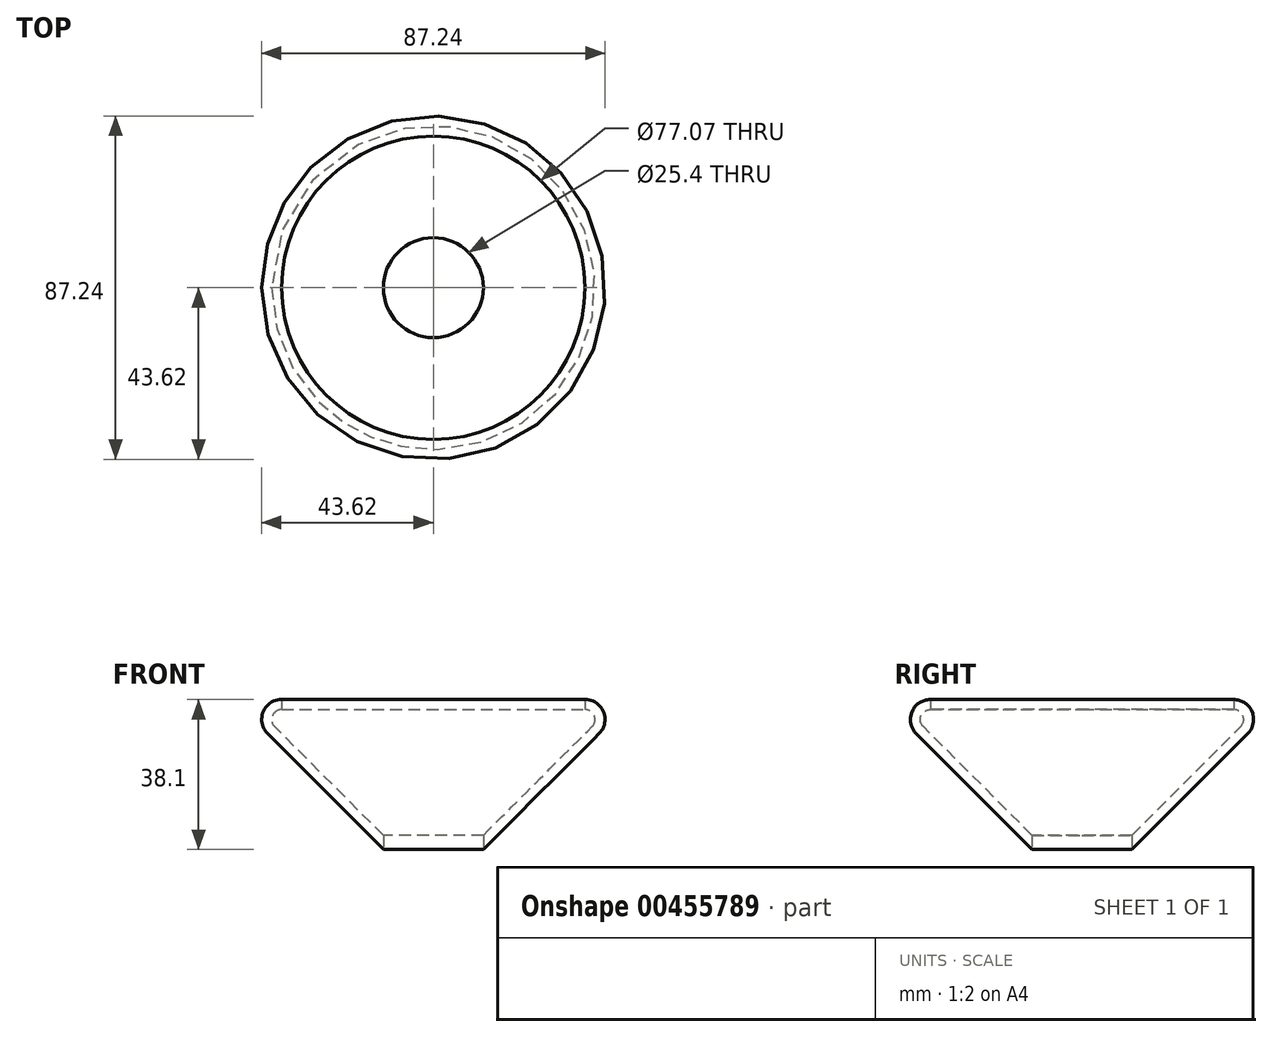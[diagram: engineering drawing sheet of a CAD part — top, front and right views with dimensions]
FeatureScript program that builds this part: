
annotation { "Feature Type Name" : "Feature", "Feature Type Description" : "" }
export const myFeature = defineFeature(function(context is Context, id is Id, definition is map)
    precondition{}
    {
        {
            var Q0;
            Q0=qCreatedBy(makeId("Front.planeOp"),FACE);
            var sketch = newSketch(context, id + "F0", { "sketchPlane" : qUnion([Q0])});
            skLineSegment(sketch, "E0", {"start": v(0, 0) * mm, "end": v(0, 50.8) * mm});
            skLineSegment(sketch, "E1", {"start": v(0, 50.8) * mm, "end": v(50.8, 50.8) * mm});
            skLineSegment(sketch, "E2", {"start": v(0, 0) * mm, "end": v(50.8, 50.8) * mm});
            skSolve(sketch);
        }
        {
            var Q0;
            Q0=makeQuery(id+"F0.imprint","IMPRINT",FACE,{"disambiguationData":[TD([[makeQuery(id+"F0.imprint","IMPRINT",EDGE,{"derivedFrom":sQuery(id+"F0.wireOp",EDGE,"E0")}),-1.0]])]});
            var Q1;
            Q1=sQuery(id+"F0.wireOp",EDGE,"E0");
            revolve(context, id + "F1", {"entities" : qUnion([Q0]), "axis" : qUnion([Q1]), "revolveType" : RevolveType.FULL});
        }
        {
            var Q0;
            Q0=makeQuery(id+"F1.opRevolve","SWEPT_EDGE",EDGE,{"disambiguationData":[OSD([sQuery(id+"F0.wireOp",EDGE,"E1"),sQuery(id+"F0.wireOp",EDGE,"E2")])]});
            fillet(context, id + "F2", {"entities" : qUnion([Q0]), "radius" : 5.08 * mm, "tangentPropagation" : true, "allowEdgeOverflow" : false});
        }
        {
            var Q0;
            Q0=makeQuery(id+"F1.opRevolve","SWEPT_FACE",FACE,{"disambiguationData":[OSD([sQuery(id+"F0.wireOp",EDGE,"E1")])]});
            shell(context, id + "F3", {"entities" : qUnion([Q0]), "thickness" : 2.54 * mm});
        }
        {
            var Q0;
            Q0=qCreatedBy(makeId("Top.planeOp"),FACE);
            var sketch = newSketch(context, id + "F4", { "sketchPlane" : qUnion([Q0])});
            skPoint(sketch, "E3", {"position": v(0, 0) * mm});
            skSolve(sketch);
        }
        {
            var Q0;
            Q0=sQuery(id+"F4.wireOp",VERTEX,"E3");
            var Q1;
            Q1=makeQuery(id+"F1.opRevolve","SWEPT_BODY",BODY,{"disambiguationData":[OSD([sQuery(id+"F0.wireOp",EDGE,"E0"),sQuery(id+"F0.wireOp",EDGE,"E1"),sQuery(id+"F0.wireOp",EDGE,"E2")])]});
            hole(context, id + "F5", {"style" : HoleStyle.SIMPLE, "endStyle" : HoleEndStyle.THROUGH, "oppositeDirection" : true, "holeDiameter" : 25.4 * mm, "isTappedThrough" : true, "tappedDepth" : 12.7 * mm, "tapClearance" : 3, "locations" : qUnion([Q0]), "scope" : qUnion([Q1])});
        }
    });
